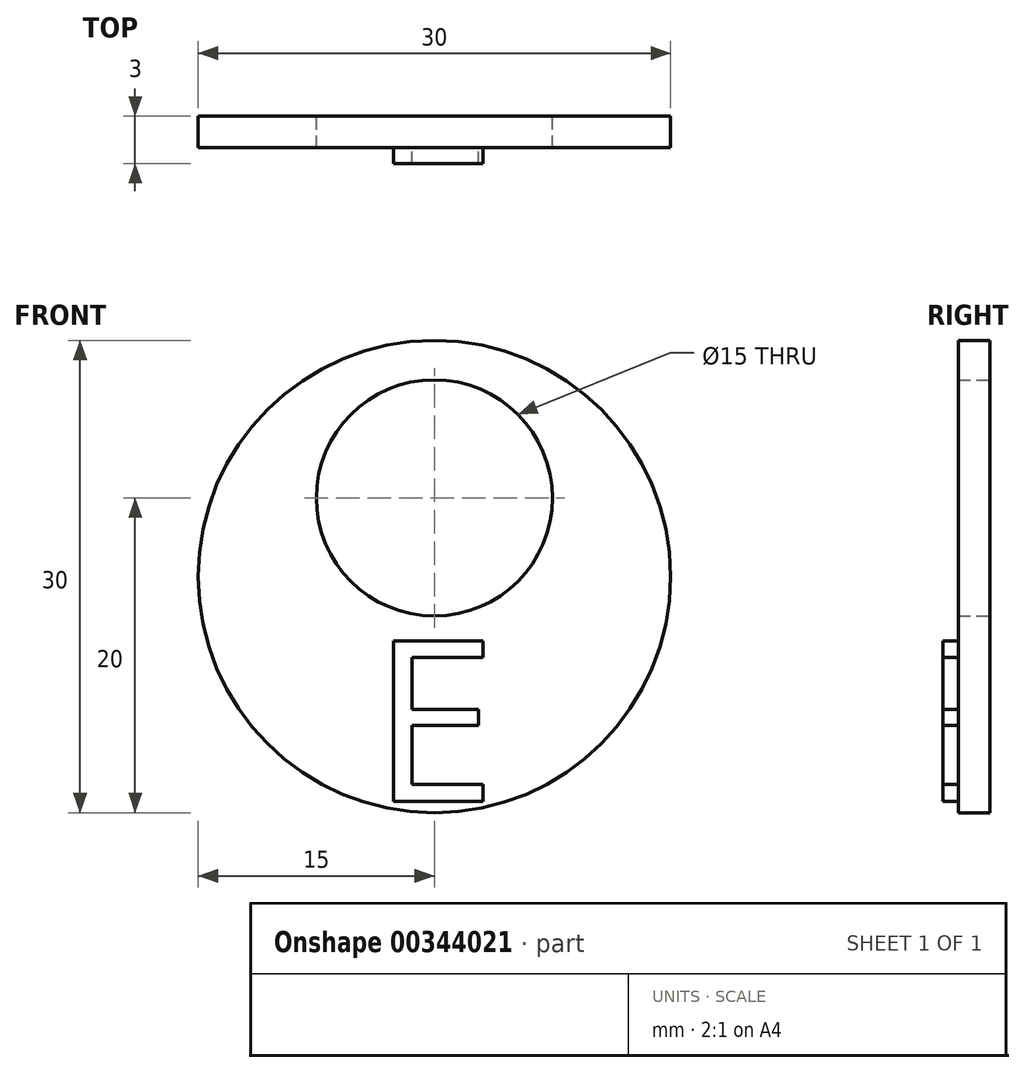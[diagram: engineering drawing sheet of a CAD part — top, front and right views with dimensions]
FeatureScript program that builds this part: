
annotation { "Feature Type Name" : "Feature", "Feature Type Description" : "" }
export const myFeature = defineFeature(function(context is Context, id is Id, definition is map)
    precondition{}
    {
        {
            var Q0;
            Q0=qCreatedBy(makeId("Front.planeOp"),FACE);
            var sketch = newSketch(context, id + "F0", { "sketchPlane" : qUnion([Q0])});
            skCircle(sketch, "E0", {"center": v(0, 0) * mm, "radius": 15 * mm});
            skPoint(sketch, "E1", {"position": v(0, 5) * mm});
            skCircle(sketch, "E2", {"center": v(0, 5) * mm, "radius": 7.5 * mm});
            skSolve(sketch);
        }
        {
            var Q0;
            Q0=makeQuery(id+"F0.imprint","IMPRINT",FACE,{"disambiguationData":[TD([[makeQuery(id+"F0.imprint","IMPRINT",EDGE,{"derivedFrom":sQuery(id+"F0.wireOp",EDGE,"E0")}),1.0]])]});
            extrude(context, id + "F1", {"entities" : qUnion([Q0]), "depth" : 2 * mm});
        }
        {
            var Q0;
            Q0=makeQuery(id+"F1.opExtrude","CAP_FACE",FACE,{"disambiguationData":[OSD([sQuery(id+"F0.wireOp",EDGE,"E0"),sQuery(id+"F0.wireOp",EDGE,"E2")])],"isStart":false});
            var sketch = newSketch(context, id + "F2", { "sketchPlane" : qUnion([Q0])});
            skText(sketch, "E3", { "text": "E", "fontName": "OpenSans-Regular.ttf"});
            const initialGuessF2  = {"E3": [-0.004, -0.01427, 1, 0, 0.01027]};
            skSetInitialGuess(sketch, initialGuessF2);
            skSolve(sketch);
        }
        {
            var Q0;
            Q0 = qSketchRegion(id + "F2", true);
            extrude(context, id + "F3", {"entities" : qUnion([Q0]), "operationType" : NewBodyOperationType.ADD, "depth" : 1 * mm});
        }
    });
